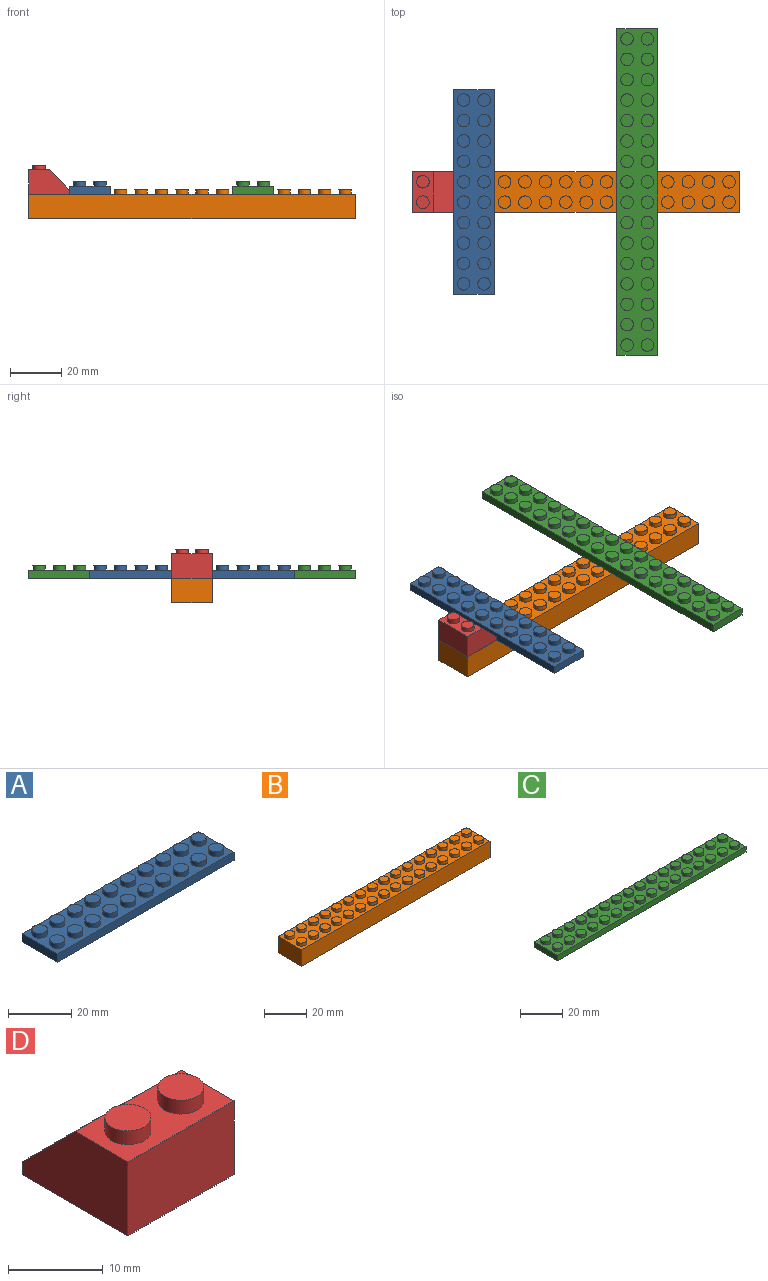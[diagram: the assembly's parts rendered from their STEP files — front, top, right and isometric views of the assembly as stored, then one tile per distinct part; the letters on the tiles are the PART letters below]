
ASSEMBLY  parts=4 mates=9
PART A: 46 faces, bbox 79.3x15.9x5 mm
  f0: cylinder r=2.44mm len=4.87mm, axis (0,0,-1), area 27.2mm2, adj f1,f42
  f1: plane 4.87x4.87mm, normal (0,0,1), area 18.6mm2, adj f0
  f2: cylinder r=2.44mm len=4.87mm, axis (0,0,-1), area 27.2mm2, adj f3,f42
  f3: plane 4.87x4.87mm, normal (0,0,1), area 18.6mm2, adj f2
  f4: cylinder r=2.44mm len=4.87mm, axis (0,0,-1), area 27.2mm2, adj f5,f42
  f5: plane 4.87x4.87mm, normal (0,0,1), area 18.6mm2, adj f4
  f6: cylinder r=2.44mm len=4.87mm, axis (0,0,-1), area 27.2mm2, adj f7,f42
  f7: plane 4.87x4.87mm, normal (0,0,1), area 18.6mm2, adj f6
  f8: cylinder r=2.44mm len=4.87mm, axis (0,0,-1), area 27.2mm2, adj f9,f42
  f9: plane 4.87x4.87mm, normal (0,0,1), area 18.6mm2, adj f8
  f10: cylinder r=2.44mm len=4.87mm, axis (0,0,-1), area 27.2mm2, adj f11,f42
  f11: plane 4.87x4.87mm, normal (0,0,1), area 18.6mm2, adj f10
  f12: cylinder r=2.44mm len=4.87mm, axis (0,0,-1), area 27.2mm2, adj f13,f42
  f13: plane 4.87x4.87mm, normal (0,0,1), area 18.6mm2, adj f12
  f14: cylinder r=2.44mm len=4.87mm, axis (0,0,-1), area 27.2mm2, adj f15,f42
  f15: plane 4.87x4.87mm, normal (0,0,1), area 18.6mm2, adj f14
  f16: cylinder r=2.44mm len=4.87mm, axis (0,0,-1), area 27.2mm2, adj f17,f42
  f17: plane 4.87x4.87mm, normal (0,0,1), area 18.6mm2, adj f16
  f18: cylinder r=2.44mm len=4.87mm, axis (0,0,-1), area 27.2mm2, adj f19,f42
  f19: plane 4.87x4.87mm, normal (0,0,1), area 18.6mm2, adj f18
  f20: cylinder r=2.44mm len=4.87mm, axis (0,0,-1), area 27.2mm2, adj f21,f42
  f21: plane 4.87x4.87mm, normal (0,0,1), area 18.6mm2, adj f20
  f22: cylinder r=2.44mm len=4.87mm, axis (0,0,-1), area 27.2mm2, adj f23,f42
  f23: plane 4.87x4.87mm, normal (0,0,1), area 18.6mm2, adj f22
  f24: cylinder r=2.44mm len=4.87mm, axis (0,0,-1), area 27.2mm2, adj f25,f42
  f25: plane 4.87x4.87mm, normal (0,0,1), area 18.6mm2, adj f24
  f26: cylinder r=2.44mm len=4.87mm, axis (0,0,-1), area 27.2mm2, adj f27,f42
  f27: plane 4.87x4.87mm, normal (0,0,1), area 18.6mm2, adj f26
  f28: cylinder r=2.44mm len=4.87mm, axis (0,0,-1), area 27.2mm2, adj f29,f42
  f29: plane 4.87x4.87mm, normal (0,0,1), area 18.6mm2, adj f28
  f30: cylinder r=2.44mm len=4.87mm, axis (0,0,-1), area 27.2mm2, adj f31,f42
  f31: plane 4.87x4.87mm, normal (0,0,1), area 18.6mm2, adj f30
  f32: cylinder r=2.44mm len=4.87mm, axis (0,0,-1), area 27.2mm2, adj f33,f42
  f33: plane 4.87x4.87mm, normal (0,0,1), area 18.6mm2, adj f32
  f34: cylinder r=2.44mm len=4.87mm, axis (0,0,-1), area 27.2mm2, adj f35,f42
  f35: plane 4.87x4.87mm, normal (0,0,1), area 18.6mm2, adj f34
  f36: cylinder r=2.44mm len=4.87mm, axis (0,0,-1), area 27.2mm2, adj f37,f42
  f37: plane 4.87x4.87mm, normal (0,0,1), area 18.6mm2, adj f36
  f38: plane 79.3x3.19mm, normal (0,-1,0), area 253mm2, adj f39,f41,f42,f43
  f39: plane 15.86x3.19mm, normal (1,0,0), area 50.6mm2, adj f38,f40,f42,f43
  f40: plane 79.3x3.19mm, normal (0,1,0), area 253mm2, adj f39,f41,f42,f43
  f41: plane 15.86x3.19mm, normal (-1,0,0), area 50.6mm2, adj f38,f40,f42,f43
  f42: plane 79.3x15.86mm, normal (0,0,1), area 885.2mm2, adj f0,f2,f4,f6,f8,f10,f12,f14
  f43: plane 79.3x15.86mm, normal (0,0,-1), area 1257.7mm2, adj f38,f39,f40,f41
  f44: cylinder r=2.44mm len=4.87mm, axis (0,0,-1), area 27.2mm2, adj f42,f45
  f45: plane 4.87x4.87mm, normal (0,0,1), area 18.6mm2, adj f44
PART B: 70 faces, bbox 126.9x15.9x11.4 mm
  f0: cylinder r=2.44mm len=4.87mm, axis (0,0,-1), area 27.2mm2, adj f1,f66
  f1: plane 4.87x4.87mm, normal (0,0,1), area 18.6mm2, adj f0
  f2: cylinder r=2.44mm len=4.87mm, axis (0,0,-1), area 27.2mm2, adj f3,f66
  f3: plane 4.87x4.87mm, normal (0,0,1), area 18.6mm2, adj f2
  f4: cylinder r=2.44mm len=4.87mm, axis (0,0,-1), area 27.2mm2, adj f5,f66
  f5: plane 4.87x4.87mm, normal (0,0,1), area 18.6mm2, adj f4
  f6: cylinder r=2.44mm len=4.87mm, axis (0,0,-1), area 27.2mm2, adj f7,f66
  f7: plane 4.87x4.87mm, normal (0,0,1), area 18.6mm2, adj f6
  f8: cylinder r=2.44mm len=4.87mm, axis (0,0,-1), area 27.2mm2, adj f9,f66
  f9: plane 4.87x4.87mm, normal (0,0,1), area 18.6mm2, adj f8
  f10: cylinder r=2.44mm len=4.87mm, axis (0,0,-1), area 27.2mm2, adj f11,f66
  f11: plane 4.87x4.87mm, normal (0,0,1), area 18.6mm2, adj f10
  f12: cylinder r=2.44mm len=4.87mm, axis (0,0,-1), area 27.2mm2, adj f13,f66
  f13: plane 4.87x4.87mm, normal (0,0,1), area 18.6mm2, adj f12
  f14: cylinder r=2.44mm len=4.87mm, axis (0,0,-1), area 27.2mm2, adj f15,f66
  f15: plane 4.87x4.87mm, normal (0,0,1), area 18.6mm2, adj f14
  f16: cylinder r=2.44mm len=4.87mm, axis (0,0,-1), area 27.2mm2, adj f17,f66
  f17: plane 4.87x4.87mm, normal (0,0,1), area 18.6mm2, adj f16
  f18: cylinder r=2.44mm len=4.87mm, axis (0,0,-1), area 27.2mm2, adj f19,f66
  f19: plane 4.87x4.87mm, normal (0,0,1), area 18.6mm2, adj f18
  f20: cylinder r=2.44mm len=4.87mm, axis (0,0,-1), area 27.2mm2, adj f21,f66
  f21: plane 4.87x4.87mm, normal (0,0,1), area 18.6mm2, adj f20
  f22: cylinder r=2.44mm len=4.87mm, axis (0,0,-1), area 27.2mm2, adj f23,f66
  f23: plane 4.87x4.87mm, normal (0,0,1), area 18.6mm2, adj f22
  f24: cylinder r=2.44mm len=4.87mm, axis (0,0,-1), area 27.2mm2, adj f25,f66
  f25: plane 4.87x4.87mm, normal (0,0,1), area 18.6mm2, adj f24
  f26: cylinder r=2.44mm len=4.87mm, axis (0,0,-1), area 27.2mm2, adj f27,f66
  f27: plane 4.87x4.87mm, normal (0,0,1), area 18.6mm2, adj f26
  f28: cylinder r=2.44mm len=4.87mm, axis (0,0,-1), area 27.2mm2, adj f29,f66
  f29: plane 4.87x4.87mm, normal (0,0,1), area 18.6mm2, adj f28
  f30: cylinder r=2.44mm len=4.87mm, axis (0,0,-1), area 27.2mm2, adj f31,f66
  f31: plane 4.87x4.87mm, normal (0,0,1), area 18.6mm2, adj f30
  f32: cylinder r=2.44mm len=4.87mm, axis (0,0,-1), area 27.2mm2, adj f33,f66
  f33: plane 4.87x4.87mm, normal (0,0,1), area 18.6mm2, adj f32
  f34: cylinder r=2.44mm len=4.87mm, axis (0,0,-1), area 27.2mm2, adj f35,f66
  f35: plane 4.87x4.87mm, normal (0,0,1), area 18.6mm2, adj f34
  f36: cylinder r=2.44mm len=4.87mm, axis (0,0,-1), area 27.2mm2, adj f37,f66
  f37: plane 4.87x4.87mm, normal (0,0,1), area 18.6mm2, adj f36
  f38: cylinder r=2.44mm len=4.87mm, axis (0,0,-1), area 27.2mm2, adj f39,f66
  f39: plane 4.87x4.87mm, normal (0,0,1), area 18.6mm2, adj f38
  f40: cylinder r=2.44mm len=4.87mm, axis (0,0,-1), area 27.2mm2, adj f41,f66
  f41: plane 4.87x4.87mm, normal (0,0,1), area 18.6mm2, adj f40
  f42: cylinder r=2.44mm len=4.87mm, axis (0,0,-1), area 27.2mm2, adj f43,f66
  f43: plane 4.87x4.87mm, normal (0,0,1), area 18.6mm2, adj f42
  f44: cylinder r=2.44mm len=4.87mm, axis (0,0,-1), area 27.2mm2, adj f45,f66
  f45: plane 4.87x4.87mm, normal (0,0,1), area 18.6mm2, adj f44
  f46: cylinder r=2.44mm len=4.87mm, axis (0,0,-1), area 27.2mm2, adj f47,f66
  f47: plane 4.87x4.87mm, normal (0,0,1), area 18.6mm2, adj f46
  f48: cylinder r=2.44mm len=4.87mm, axis (0,0,-1), area 27.2mm2, adj f49,f66
  f49: plane 4.87x4.87mm, normal (0,0,1), area 18.6mm2, adj f48
  f50: cylinder r=2.44mm len=4.87mm, axis (0,0,-1), area 27.2mm2, adj f51,f66
  f51: plane 4.87x4.87mm, normal (0,0,1), area 18.6mm2, adj f50
  f52: cylinder r=2.44mm len=4.87mm, axis (0,0,-1), area 27.2mm2, adj f53,f66
  f53: plane 4.87x4.87mm, normal (0,0,1), area 18.6mm2, adj f52
  f54: cylinder r=2.44mm len=4.87mm, axis (0,0,-1), area 27.2mm2, adj f55,f66
  f55: plane 4.87x4.87mm, normal (0,0,1), area 18.6mm2, adj f54
  f56: cylinder r=2.44mm len=4.87mm, axis (0,0,-1), area 27.2mm2, adj f57,f66
  f57: plane 4.87x4.87mm, normal (0,0,1), area 18.6mm2, adj f56
  f58: cylinder r=2.44mm len=4.87mm, axis (0,0,-1), area 27.2mm2, adj f59,f66
  f59: plane 4.87x4.87mm, normal (0,0,1), area 18.6mm2, adj f58
  f60: cylinder r=2.44mm len=4.87mm, axis (0,0,-1), area 27.2mm2, adj f61,f66
  f61: plane 4.87x4.87mm, normal (0,0,1), area 18.6mm2, adj f60
  f62: plane 126.88x9.57mm, normal (0,-1,0), area 1214.2mm2, adj f63,f65,f66,f67
  f63: plane 15.86x9.57mm, normal (1,0,0), area 151.8mm2, adj f62,f64,f66,f67
  f64: plane 126.88x9.57mm, normal (0,1,0), area 1214.2mm2, adj f63,f65,f66,f67
  f65: plane 15.86x9.57mm, normal (-1,0,0), area 151.8mm2, adj f62,f64,f66,f67
  f66: plane 126.88x15.86mm, normal (0,0,1), area 1416.2mm2, adj f0,f2,f4,f6,f8,f10,f12,f14
  f67: plane 126.88x15.86mm, normal (0,0,-1), area 2012.3mm2, adj f62,f63,f64,f65
  f68: cylinder r=2.44mm len=4.87mm, axis (0,0,-1), area 27.2mm2, adj f66,f69
  f69: plane 4.87x4.87mm, normal (0,0,1), area 18.6mm2, adj f68
PART C: 70 faces, bbox 126.9x15.9x5 mm
  f0: cylinder r=2.44mm len=4.87mm, axis (0,0,-1), area 27.2mm2, adj f1,f66
  f1: plane 4.87x4.87mm, normal (0,0,1), area 18.6mm2, adj f0
  f2: cylinder r=2.44mm len=4.87mm, axis (0,0,-1), area 27.2mm2, adj f3,f66
  f3: plane 4.87x4.87mm, normal (0,0,1), area 18.6mm2, adj f2
  f4: cylinder r=2.44mm len=4.87mm, axis (0,0,-1), area 27.2mm2, adj f5,f66
  f5: plane 4.87x4.87mm, normal (0,0,1), area 18.6mm2, adj f4
  f6: cylinder r=2.44mm len=4.87mm, axis (0,0,-1), area 27.2mm2, adj f7,f66
  f7: plane 4.87x4.87mm, normal (0,0,1), area 18.6mm2, adj f6
  f8: cylinder r=2.44mm len=4.87mm, axis (0,0,-1), area 27.2mm2, adj f9,f66
  f9: plane 4.87x4.87mm, normal (0,0,1), area 18.6mm2, adj f8
  f10: cylinder r=2.44mm len=4.87mm, axis (0,0,-1), area 27.2mm2, adj f11,f66
  f11: plane 4.87x4.87mm, normal (0,0,1), area 18.6mm2, adj f10
  f12: cylinder r=2.44mm len=4.87mm, axis (0,0,-1), area 27.2mm2, adj f13,f66
  f13: plane 4.87x4.87mm, normal (0,0,1), area 18.6mm2, adj f12
  f14: cylinder r=2.44mm len=4.87mm, axis (0,0,-1), area 27.2mm2, adj f15,f66
  f15: plane 4.87x4.87mm, normal (0,0,1), area 18.6mm2, adj f14
  f16: cylinder r=2.44mm len=4.87mm, axis (0,0,-1), area 27.2mm2, adj f17,f66
  f17: plane 4.87x4.87mm, normal (0,0,1), area 18.6mm2, adj f16
  f18: cylinder r=2.44mm len=4.87mm, axis (0,0,-1), area 27.2mm2, adj f19,f66
  f19: plane 4.87x4.87mm, normal (0,0,1), area 18.6mm2, adj f18
  f20: cylinder r=2.44mm len=4.87mm, axis (0,0,-1), area 27.2mm2, adj f21,f66
  f21: plane 4.87x4.87mm, normal (0,0,1), area 18.6mm2, adj f20
  f22: cylinder r=2.44mm len=4.87mm, axis (0,0,-1), area 27.2mm2, adj f23,f66
  f23: plane 4.87x4.87mm, normal (0,0,1), area 18.6mm2, adj f22
  f24: cylinder r=2.44mm len=4.87mm, axis (0,0,-1), area 27.2mm2, adj f25,f66
  f25: plane 4.87x4.87mm, normal (0,0,1), area 18.6mm2, adj f24
  f26: cylinder r=2.44mm len=4.87mm, axis (0,0,-1), area 27.2mm2, adj f27,f66
  f27: plane 4.87x4.87mm, normal (0,0,1), area 18.6mm2, adj f26
  f28: cylinder r=2.44mm len=4.87mm, axis (0,0,-1), area 27.2mm2, adj f29,f66
  f29: plane 4.87x4.87mm, normal (0,0,1), area 18.6mm2, adj f28
  f30: cylinder r=2.44mm len=4.87mm, axis (0,0,-1), area 27.2mm2, adj f31,f66
  f31: plane 4.87x4.87mm, normal (0,0,1), area 18.6mm2, adj f30
  f32: cylinder r=2.44mm len=4.87mm, axis (0,0,-1), area 27.2mm2, adj f33,f66
  f33: plane 4.87x4.87mm, normal (0,0,1), area 18.6mm2, adj f32
  f34: cylinder r=2.44mm len=4.87mm, axis (0,0,-1), area 27.2mm2, adj f35,f66
  f35: plane 4.87x4.87mm, normal (0,0,1), area 18.6mm2, adj f34
  f36: cylinder r=2.44mm len=4.87mm, axis (0,0,-1), area 27.2mm2, adj f37,f66
  f37: plane 4.87x4.87mm, normal (0,0,1), area 18.6mm2, adj f36
  f38: cylinder r=2.44mm len=4.87mm, axis (0,0,-1), area 27.2mm2, adj f39,f66
  f39: plane 4.87x4.87mm, normal (0,0,1), area 18.6mm2, adj f38
  f40: cylinder r=2.44mm len=4.87mm, axis (0,0,-1), area 27.2mm2, adj f41,f66
  f41: plane 4.87x4.87mm, normal (0,0,1), area 18.6mm2, adj f40
  f42: cylinder r=2.44mm len=4.87mm, axis (0,0,-1), area 27.2mm2, adj f43,f66
  f43: plane 4.87x4.87mm, normal (0,0,1), area 18.6mm2, adj f42
  f44: cylinder r=2.44mm len=4.87mm, axis (0,0,-1), area 27.2mm2, adj f45,f66
  f45: plane 4.87x4.87mm, normal (0,0,1), area 18.6mm2, adj f44
  f46: cylinder r=2.44mm len=4.87mm, axis (0,0,-1), area 27.2mm2, adj f47,f66
  f47: plane 4.87x4.87mm, normal (0,0,1), area 18.6mm2, adj f46
  f48: cylinder r=2.44mm len=4.87mm, axis (0,0,-1), area 27.2mm2, adj f49,f66
  f49: plane 4.87x4.87mm, normal (0,0,1), area 18.6mm2, adj f48
  f50: cylinder r=2.44mm len=4.87mm, axis (0,0,-1), area 27.2mm2, adj f51,f66
  f51: plane 4.87x4.87mm, normal (0,0,1), area 18.6mm2, adj f50
  f52: cylinder r=2.44mm len=4.87mm, axis (0,0,-1), area 27.2mm2, adj f53,f66
  f53: plane 4.87x4.87mm, normal (0,0,1), area 18.6mm2, adj f52
  f54: cylinder r=2.44mm len=4.87mm, axis (0,0,-1), area 27.2mm2, adj f55,f66
  f55: plane 4.87x4.87mm, normal (0,0,1), area 18.6mm2, adj f54
  f56: cylinder r=2.44mm len=4.87mm, axis (0,0,-1), area 27.2mm2, adj f57,f66
  f57: plane 4.87x4.87mm, normal (0,0,1), area 18.6mm2, adj f56
  f58: cylinder r=2.44mm len=4.87mm, axis (0,0,-1), area 27.2mm2, adj f59,f66
  f59: plane 4.87x4.87mm, normal (0,0,1), area 18.6mm2, adj f58
  f60: cylinder r=2.44mm len=4.87mm, axis (0,0,-1), area 27.2mm2, adj f61,f66
  f61: plane 4.87x4.87mm, normal (0,0,1), area 18.6mm2, adj f60
  f62: plane 126.88x3.19mm, normal (0,-1,0), area 404.7mm2, adj f63,f65,f66,f67
  f63: plane 15.86x3.19mm, normal (1,0,0), area 50.6mm2, adj f62,f64,f66,f67
  f64: plane 126.88x3.19mm, normal (0,1,0), area 404.7mm2, adj f63,f65,f66,f67
  f65: plane 15.86x3.19mm, normal (-1,0,0), area 50.6mm2, adj f62,f64,f66,f67
  f66: plane 126.88x15.86mm, normal (0,0,1), area 1416.2mm2, adj f0,f2,f4,f6,f8,f10,f12,f14
  f67: plane 126.88x15.86mm, normal (0,0,-1), area 2012.3mm2, adj f62,f63,f64,f65
  f68: cylinder r=2.44mm len=4.87mm, axis (0,0,-1), area 27.2mm2, adj f66,f69
  f69: plane 4.87x4.87mm, normal (0,0,1), area 18.6mm2, adj f68
PART D: 11 faces, bbox 15.9x15.9x11.4 mm
  f0: plane 15.86x9.57mm, normal (1,0,0), area 120.3mm2, adj f3,f4,f6,f7,f10
  f1: cylinder r=2.44mm len=4.87mm, axis (0,0,-1), area 27.2mm2, adj f2,f6
  f2: plane 4.87x4.87mm, normal (0,0,1), area 18.6mm2, adj f1
  f3: plane 15.86x9.57mm, normal (0,-1,0), area 151.8mm2, adj f0,f5,f6,f7
  f4: plane 15.86x1.64mm, normal (0,1,0), area 26mm2, adj f0,f5,f7,f10
  f5: plane 15.86x9.57mm, normal (-1,0,0), area 120.3mm2, adj f3,f4,f6,f7,f10
  f6: plane 15.86x7.93mm, normal (0,0,1), area 88.5mm2, adj f0,f1,f3,f5,f8,f10
  f7: plane 15.86x15.86mm, normal (0,0,-1), area 251.5mm2, adj f0,f3,f4,f5
  f8: cylinder r=2.44mm len=4.87mm, axis (0,0,-1), area 27.2mm2, adj f6,f9
  f9: plane 4.87x4.87mm, normal (0,0,1), area 18.6mm2, adj f8
  f10: plane 15.86x7.93mm, normal (0,0.71,0.71), area 177.9mm2, adj f0,f4,f5,f6
PLACE A rot(axis=(0,0,-1),90deg) t=(-39.65,0,9.57)mm
PLACE B at identity fixed
PLACE C rot(axis=(0,0,-1),90deg) t=(23.79,0,9.57)mm
PLACE D rot(axis=(0,0,-1),90deg) t=(-55.51,0,9.57)mm
MATE planar D.f7 <-> B.f66  axis (0,0,-1) through (-55.51,0,9.57)mm
MATE planar C.f67 <-> B.f66  axis (0,0,-1) through (23.79,0,9.57)mm
MATE cylindrical D.f1 <-> B.f68  axis (0,0,1) through (-59.47,-3.97,20.92)mm
MATE cylindrical C.f28 <-> B.f18  axis (0,0,1) through (27.76,-3.96,14.54)mm
MATE parallel D.f3 <-> B.f65  axis (-1,0,0) through (-63.44,0,14.36)mm
MATE cylindrical A.f18 <-> B.f54  axis (0,0,-1) through (-43.61,-3.97,13.65)mm
MATE parallel B.f65 <-> C.f62  axis (-1,0,0) through (-63.44,0,4.79)mm
MATE planar B.f66 <-> A.f43  axis (0,0,1) through (0,0,9.57)mm
MATE parallel A.f38 <-> B.f65  axis (-1,0,0) through (-47.58,0,11.17)mm
